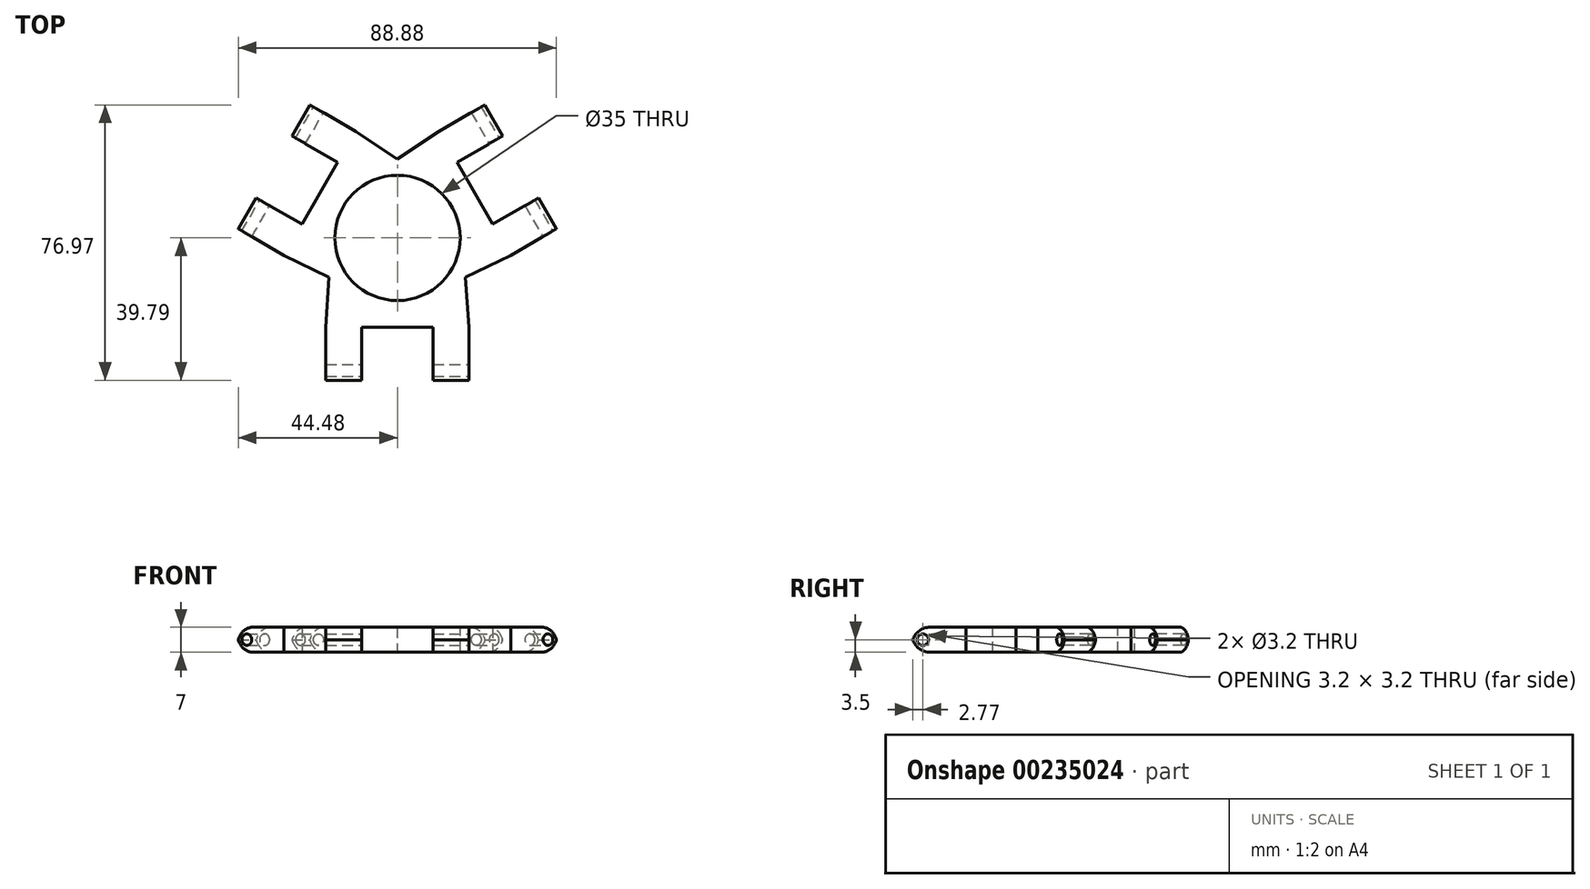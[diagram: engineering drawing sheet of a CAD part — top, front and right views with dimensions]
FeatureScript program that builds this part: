
annotation { "Feature Type Name" : "Feature", "Feature Type Description" : "" }
export const myFeature = defineFeature(function(context is Context, id is Id, definition is map)
    precondition{}
    {
        {
            var Q0;
            Q0=qCreatedBy(makeId("Top.planeOp"),FACE);
            var sketch = newSketch(context, id + "F0", { "sketchPlane" : qUnion([Q0])});
            skLineSegment(sketch, "E0", {"start": v(-0.04, -0.02) * mm, "end": v(-21.7, 12.48) * mm});
            skLineSegment(sketch, "E1", {"start": v(-21.7, 12.48) * mm, "end": v(-11.7, 29.8) * mm});
            skLineSegment(sketch, "E2", {"start": v(-21.7, 12.48) * mm, "end": v(-31.7, -4.84) * mm});
            skLineSegment(sketch, "E3", {"start": v(-0.04, -0.02) * mm, "end": v(21.6, 12.48) * mm});
            skLineSegment(sketch, "E4", {"start": v(-0.04, -0.02) * mm, "end": v(-0.04, -25.02) * mm});
            skLineSegment(sketch, "E5", {"start": v(-0.04, -25.02) * mm, "end": v(-20.04, -25.02) * mm});
            skLineSegment(sketch, "E6", {"start": v(-0.04, -25.02) * mm, "end": v(19.96, -25.02) * mm});
            skLineSegment(sketch, "E7", {"start": v(21.6, 12.48) * mm, "end": v(31.6, -4.84) * mm});
            skLineSegment(sketch, "E8", {"start": v(21.6, 12.48) * mm, "end": v(11.6, 29.8) * mm});
            skLineSegment(sketch, "E9.bottom", {"start": v(-31.7, -4.84) * mm, "end": v(-26.7, 3.82) * mm});
            skLineSegment(sketch, "E9.top", {"start": v(-44.68, 2.66) * mm, "end": v(-39.68, 11.32) * mm});
            skLineSegment(sketch, "E9.left", {"start": v(-31.7, -4.84) * mm, "end": v(-44.68, 2.66) * mm});
            skLineSegment(sketch, "E9.right", {"start": v(-26.7, 3.82) * mm, "end": v(-39.68, 11.32) * mm});
            skLineSegment(sketch, "E10.bottom", {"start": v(-11.7, 29.8) * mm, "end": v(-16.7, 21.14) * mm});
            skLineSegment(sketch, "E10.top", {"start": v(-24.68, 37.3) * mm, "end": v(-29.68, 28.64) * mm});
            skLineSegment(sketch, "E10.left", {"start": v(-11.7, 29.8) * mm, "end": v(-24.68, 37.3) * mm});
            skLineSegment(sketch, "E10.right", {"start": v(-16.7, 21.14) * mm, "end": v(-29.68, 28.64) * mm});
            skLineSegment(sketch, "E11", {"start": v(-20.04, -25.02) * mm, "end": v(-20.04, -40.02) * mm});
            skLineSegment(sketch, "E12", {"start": v(-20.04, -40.02) * mm, "end": v(-10.04, -40.02) * mm});
            skLineSegment(sketch, "E13", {"start": v(-10.04, -40.02) * mm, "end": v(-10.04, -25.02) * mm});
            skLineSegment(sketch, "E14", {"start": v(19.96, -25.02) * mm, "end": v(19.96, -40.02) * mm});
            skLineSegment(sketch, "E15", {"start": v(19.96, -40.02) * mm, "end": v(9.96, -40.02) * mm});
            skLineSegment(sketch, "E16", {"start": v(9.96, -40.02) * mm, "end": v(9.96, -25.02) * mm});
            skLineSegment(sketch, "E17", {"start": v(31.6, -4.84) * mm, "end": v(44.6, 2.66) * mm});
            skLineSegment(sketch, "E18", {"start": v(44.6, 2.66) * mm, "end": v(39.6, 11.32) * mm});
            skLineSegment(sketch, "E19", {"start": v(39.6, 11.32) * mm, "end": v(26.6, 3.82) * mm});
            skLineSegment(sketch, "E20", {"start": v(11.6, 29.8) * mm, "end": v(24.6, 37.3) * mm});
            skLineSegment(sketch, "E21", {"start": v(24.6, 37.3) * mm, "end": v(29.6, 28.64) * mm});
            skLineSegment(sketch, "E22", {"start": v(29.6, 28.64) * mm, "end": v(16.6, 21.14) * mm});
            skLineSegment(sketch, "E23", {"start": v(-0.04, -0.02) * mm, "end": v(-19.1, -11.02) * mm});
            skLineSegment(sketch, "E24", {"start": v(-0.04, -0.02) * mm, "end": v(-0.04, 21.98) * mm});
            skLineSegment(sketch, "E25", {"start": v(-0.04, -0.02) * mm, "end": v(19.01, -11.02) * mm});
            skLineSegment(sketch, "E26", {"start": v(19.01, -11.02) * mm, "end": v(31.6, -4.84) * mm});
            skLineSegment(sketch, "E27", {"start": v(19.96, -25.02) * mm, "end": v(19.01, -11.02) * mm});
            skLineSegment(sketch, "E28", {"start": v(-20.04, -25.02) * mm, "end": v(-19.1, -11.02) * mm});
            skLineSegment(sketch, "E29", {"start": v(-31.7, -4.84) * mm, "end": v(-19.1, -11.02) * mm});
            skLineSegment(sketch, "E30", {"start": v(-11.7, 29.8) * mm, "end": v(-0.04, 21.98) * mm});
            skLineSegment(sketch, "E31", {"start": v(11.6, 29.8) * mm, "end": v(-0.04, 21.98) * mm});
            skSolve(sketch);
        }
        {
            var Q0;
            Q0 = qSketchRegion(id + "F0", true);
            extrude(context, id + "F1", {"entities" : qUnion([Q0]), "depth" : 7 * mm});
        }
        {
            var Q0;
            Q0=makeQuery(id+"F1.opExtrude","SWEPT_FACE",FACE,{"disambiguationData":[OSD([sQuery(id+"F0.wireOp",EDGE,"E14")])]});
            var sketch = newSketch(context, id + "F2", { "sketchPlane" : qUnion([Q0])});
            skLineSegment(sketch, "E32", {"start": v(-40.02, 3.5) * mm, "end": v(-37.02, 3.5) * mm});
            skCircle(sketch, "E33", {"center": v(-37.02, 3.5) * mm, "radius": 1.6 * mm});
            skSolve(sketch);
        }
        {
            var Q0;
            {var subQ0=sQuery(id+"F2.wireOp",EDGE,"hwxsNGN8-YZ7C-MMK4-pKxF-B9U5Xw8N2g3O");var subQ1=sQuery(id+"F2.wireOp",EDGE,"aEPsG9ev-R9g6-eiI9-y869-0mmje5FJimsM");var subQ2=makeQuery(id+"F2.imprint","INTERSECT",VERTEX,{"disambiguationData":[OD(0.0)],"derivedFrom":[subQ1,subQ0]});Q0=makeQuery(id+"F2.imprint","IMPRINT",FACE,{"disambiguationData":[TD([[makeQuery(id+"F2.imprint","IMPRINT",EDGE,{"disambiguationData":[TD([[subQ2,-1.0]])],"derivedFrom":subQ1}),1.0]])]});}
            var Q1;
            Q1=makeQuery(id+"F2.imprint","IMPRINT",FACE,{"disambiguationData":[TD([[makeQuery(id+"F2.imprint","IMPRINT",EDGE,{"derivedFrom":sQuery(id+"F2.wireOp",EDGE,"E33")}),1.0]])]});
            extrude(context, id + "F3", {"entities" : qUnion([Q0, Q1]), "operationType" : NewBodyOperationType.REMOVE, "oppositeDirection" : true, "depth" : 60 * mm});
        }
        {
            var Q0;
            Q0=makeQuery(id+"F1.opExtrude","SWEPT_FACE",FACE,{"disambiguationData":[OSD([sQuery(id+"F0.wireOp",EDGE,"E17")])]});
            var sketch = newSketch(context, id + "F4", { "sketchPlane" : qUnion([Q0])});
            skLineSegment(sketch, "E34", {"start": v(39.95, 3.5) * mm, "end": v(36.95, 3.5) * mm});
            skCircle(sketch, "E35", {"center": v(36.95, 3.5) * mm, "radius": 1.6 * mm});
            skSolve(sketch);
        }
        {
            var Q0;
            Q0 = qSketchRegion(id + "F4", true);
            extrude(context, id + "F5", {"entities" : qUnion([Q0]), "operationType" : NewBodyOperationType.REMOVE, "oppositeDirection" : true, "depth" : 60 * mm});
        }
        {
            var Q0;
            Q0=makeQuery(id+"F1.opExtrude","SWEPT_FACE",FACE,{"disambiguationData":[OSD([sQuery(id+"F0.wireOp",EDGE,"E10.left")])]});
            var sketch = newSketch(context, id + "F6", { "sketchPlane" : qUnion([Q0])});
            skLineSegment(sketch, "E36", {"start": v(40.03, 3.5) * mm, "end": v(37.03, 3.5) * mm});
            skCircle(sketch, "E37", {"center": v(37.03, 3.5) * mm, "radius": 1.6 * mm});
            skSolve(sketch);
        }
        {
            var Q0;
            Q0=makeQuery(id+"F6.imprint","IMPRINT",FACE,{"disambiguationData":[TD([[makeQuery(id+"F6.imprint","IMPRINT",EDGE,{"derivedFrom":sQuery(id+"F6.wireOp",EDGE,"E37")}),1.0]])]});
            extrude(context, id + "F7", {"entities" : qUnion([Q0]), "operationType" : NewBodyOperationType.REMOVE, "oppositeDirection" : true, "depth" : 60 * mm});
        }
        {
            var Q0;
            Q0=makeQuery(id+"F1.opExtrude","CAP_FACE",FACE,{"disambiguationData":[OSD([sQuery(id+"F0.wireOp",EDGE,"E1"),sQuery(id+"F0.wireOp",EDGE,"E2"),sQuery(id+"F0.wireOp",EDGE,"E5"),sQuery(id+"F0.wireOp",EDGE,"E6"),sQuery(id+"F0.wireOp",EDGE,"E7"),sQuery(id+"F0.wireOp",EDGE,"E8"),sQuery(id+"F0.wireOp",EDGE,"ogWWpCTX-pv5V-tfM1-JVI4-smtYqjHj5hic"),sQuery(id+"F0.wireOp",EDGE,"aMA2J1BL-dzu3-jsiP-cDxz-KdwlyVqdBqax"),sQuery(id+"F0.wireOp",EDGE,"ztYhUtQq-5O7m-MgnK-VJ34-YIY8iCbyuaeO"),sQuery(id+"F0.wireOp",EDGE,"E9.top"),sQuery(id+"F0.wireOp",EDGE,"E9.left"),sQuery(id+"F0.wireOp",EDGE,"E9.right"),sQuery(id+"F0.wireOp",EDGE,"E10.top"),sQuery(id+"F0.wireOp",EDGE,"E10.left"),sQuery(id+"F0.wireOp",EDGE,"E10.right"),sQuery(id+"F0.wireOp",EDGE,"E11"),sQuery(id+"F0.wireOp",EDGE,"E12"),sQuery(id+"F0.wireOp",EDGE,"E13"),sQuery(id+"F0.wireOp",EDGE,"E14"),sQuery(id+"F0.wireOp",EDGE,"E15"),sQuery(id+"F0.wireOp",EDGE,"E16"),sQuery(id+"F0.wireOp",EDGE,"E17"),sQuery(id+"F0.wireOp",EDGE,"E18"),sQuery(id+"F0.wireOp",EDGE,"E19"),sQuery(id+"F0.wireOp",EDGE,"E20"),sQuery(id+"F0.wireOp",EDGE,"E21"),sQuery(id+"F0.wireOp",EDGE,"E22")])],"isStart":false});
            var sketch = newSketch(context, id + "F8", { "sketchPlane" : qUnion([Q0])});
            skCircle(sketch, "E38", {"center": v(0, 0) * mm, "radius": 17.5 * mm});
            skSolve(sketch);
        }
        {
            var Q0;
            Q0=makeQuery(id+"F8.imprint","IMPRINT",FACE,{"disambiguationData":[TD([[makeQuery(id+"F8.imprint","IMPRINT",EDGE,{"derivedFrom":sQuery(id+"F8.wireOp",EDGE,"E38")}),1.0]])]});
            extrude(context, id + "F9", {"entities" : qUnion([Q0]), "operationType" : NewBodyOperationType.REMOVE, "oppositeDirection" : true, "depth" : 25 * mm});
        }
        {
            var Q0;
            Q0=makeQuery(id+"F1.opExtrude","CAP_EDGE",EDGE,{"disambiguationData":[OSD([sQuery(id+"F0.wireOp",EDGE,"E12")])],"isStart":false});
            var Q1;
            Q1=makeQuery(id+"F1.opExtrude","CAP_EDGE",EDGE,{"disambiguationData":[OSD([sQuery(id+"F0.wireOp",EDGE,"E12")])],"isStart":true});
            var Q2;
            Q2=makeQuery(id+"F1.opExtrude","CAP_EDGE",EDGE,{"disambiguationData":[OSD([sQuery(id+"F0.wireOp",EDGE,"E15")])],"isStart":true});
            var Q3;
            Q3=makeQuery(id+"F1.opExtrude","CAP_EDGE",EDGE,{"disambiguationData":[OSD([sQuery(id+"F0.wireOp",EDGE,"E15")])],"isStart":false});
            var Q4;
            Q4=makeQuery(id+"F1.opExtrude","CAP_EDGE",EDGE,{"disambiguationData":[OSD([sQuery(id+"F0.wireOp",EDGE,"E18")])],"isStart":false});
            var Q5;
            Q5=makeQuery(id+"F1.opExtrude","CAP_EDGE",EDGE,{"disambiguationData":[OSD([sQuery(id+"F0.wireOp",EDGE,"E18")])],"isStart":true});
            var Q6;
            Q6=makeQuery(id+"F1.opExtrude","CAP_EDGE",EDGE,{"disambiguationData":[OSD([sQuery(id+"F0.wireOp",EDGE,"E21")])],"isStart":false});
            var Q7;
            Q7=makeQuery(id+"F1.opExtrude","CAP_EDGE",EDGE,{"disambiguationData":[OSD([sQuery(id+"F0.wireOp",EDGE,"E21")])],"isStart":true});
            var Q8;
            Q8=makeQuery(id+"F1.opExtrude","CAP_EDGE",EDGE,{"disambiguationData":[OSD([sQuery(id+"F0.wireOp",EDGE,"E10.top")])],"isStart":false});
            var Q9;
            Q9=makeQuery(id+"F1.opExtrude","CAP_EDGE",EDGE,{"disambiguationData":[OSD([sQuery(id+"F0.wireOp",EDGE,"E10.top")])],"isStart":true});
            var Q10;
            Q10=makeQuery(id+"F1.opExtrude","CAP_EDGE",EDGE,{"disambiguationData":[OSD([sQuery(id+"F0.wireOp",EDGE,"E9.top")])],"isStart":false});
            var Q11;
            Q11=makeQuery(id+"F1.opExtrude","CAP_EDGE",EDGE,{"disambiguationData":[OSD([sQuery(id+"F0.wireOp",EDGE,"E9.top")])],"isStart":true});
            fillet(context, id + "F10", {"entities" : qUnion([Q0, Q1, Q2, Q3, Q4, Q5, Q6, Q7, Q8, Q9, Q10, Q11]), "radius" : 5 * mm, "tangentPropagation" : true, "allowEdgeOverflow" : false});
        }
    });
